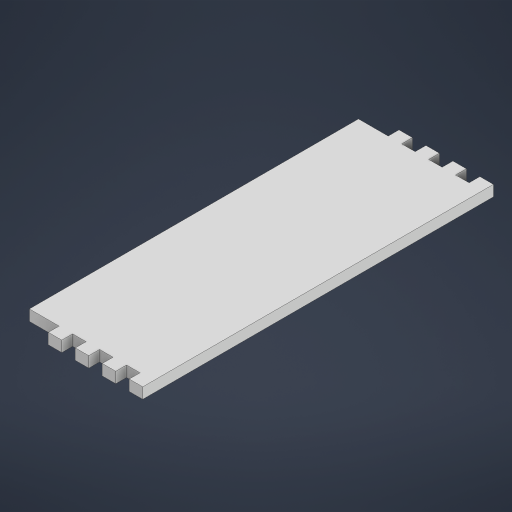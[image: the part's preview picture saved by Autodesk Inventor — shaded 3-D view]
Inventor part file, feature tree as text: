
AUTODESK INVENTOR PART (.ipt)
format: ipt  version: 2023 (Build 270158030, 158C)  size: 190,976 bytes
history: native  units: mm
features: extrude x1, sketch x1
ambient origin geometry x8: Origin, YZ Plane, XZ Plane, XY Plane, X Axis, Y Axis, Z Axis, Center Point
bodies: Solid1 (feature_tree)
feature tree (2):
  extrude  "Extrusion1"  Depth=4.0mm TaperAngle=0.0deg
  sketch  "Sketch1"  dims[d0=90.0deg d1=4.0mm d2=0.0mm]
